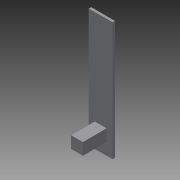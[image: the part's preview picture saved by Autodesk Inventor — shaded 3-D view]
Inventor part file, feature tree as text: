
AUTODESK INVENTOR PART (.ipt)
format: ipt  version: 2014 (Build 180170000, 170)  size: 89,600 bytes
history: native  units: in
note: dims shown in document units (in); Inventor stores cm internally (conversion verified against a paired STEP export)
features: sketch x3, extrude x2, hole x2
ambient origin geometry x8: Origin, YZ Plane, XZ Plane, XY Plane, X Axis, Y Axis, Z Axis, Center Point
bodies: Solid1 (feature_tree)
feature tree (7):
  extrude  "Extrusion1"  Depth=50.0in
  sketch  "Sketch2"  dims[d2=1.0in d3=0.0in d5=5.0in]
  hole  "Hole1"  [1 undecoded]
  extrude  "Extrusion2"  Depth=5.0in
  hole  "Hole2"  [1 undecoded]
  sketch  "Sketch1"  dims[d0=10.0in d1=50.0in]
  sketch  "Sketch3"  dims[d6=5.0in d7=5.0in d8=0.25in d9=0.75in d10=0.375in d11=0.25in d12=0.5635in d13=1.0in d14=0.8108in d15=10.0in d16=0.0in d17=8.0in d18=0.25in d19=0.75in d20=0.375in d21=0.25in d22=0.5635in d23=1.0in d24=0.8108in]
note: 2 required parameter values undecoded (feature->parameter linkage not recoverable at this tier; creation-order binding heuristic only, values carry confidence <= 0.55)
